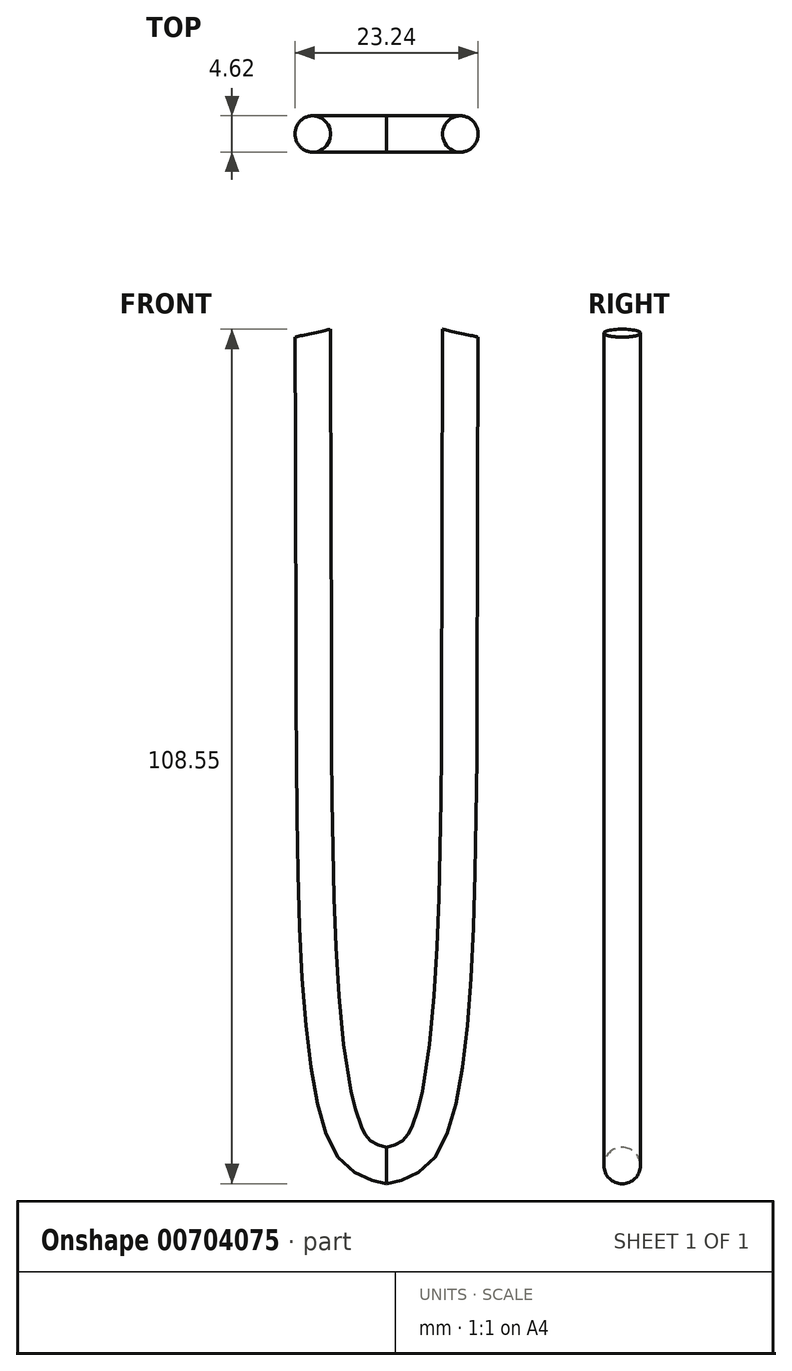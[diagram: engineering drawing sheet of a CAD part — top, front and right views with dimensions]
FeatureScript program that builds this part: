
annotation { "Feature Type Name" : "Feature", "Feature Type Description" : "" }
export const myFeature = defineFeature(function(context is Context, id is Id, definition is map)
    precondition{}
    {
        {
            var Q0;
            Q0=qCreatedBy(makeId("Front.planeOp"),FACE);
            var sketch = newSketch(context, id + "F0", { "sketchPlane" : qUnion([Q0])});
            skFitSpline(sketch, "E0", {"points": [v(0, -64) * mm, v(4.81, -60.84) * mm, v(9.25, 0) * mm, v(9.37, 41.4) * mm, v(9.37, 41.76) * mm], "startDerivative": vector(37.64, 8.71) * mm, "endDerivative": vector(-0.06, 6.2) * mm});
            skFitSpline(sketch, "E1", {"points": [v(9.25, 0) * mm, v(18.47, 12.7) * mm, v(20.22, 30.9) * mm], "startDerivative": vector(21.48, 27.26) * mm, "endDerivative": vector(-0.7, 31.79) * mm});
            skFitSpline(sketch, "E2", {"points": [v(9.08, -23.38) * mm, v(20.34, -21.27) * mm, v(24.42, -10.77) * mm], "startDerivative": vector(24.53, -3.08) * mm, "endDerivative": vector(5.87, 23.46) * mm});
            skSolve(sketch);
        }
        {
            var Q0;
            Q0=qCreatedBy(makeId("Right.planeOp"),FACE);
            var sketch = newSketch(context, id + "F1", { "sketchPlane" : qUnion([Q0])});
            skCircle(sketch, "E3", {"center": v(0, -64) * mm, "radius": 2.31 * mm});
            skSolve(sketch);
        }
        {
            var Q0;
            Q0=makeQuery(id+"F1.imprint","IMPRINT",FACE,{"disambiguationData":[TD([[makeQuery(id+"F1.imprint","IMPRINT",EDGE,{"derivedFrom":sQuery(id+"F1.wireOp",EDGE,"E3")}),1.0]])]});
            var Q1;
            Q1=sQuery(id+"F0.wireOp",EDGE,"E0");
            sweep(context, id + "F2", {"profiles" : qUnion([Q0]), "path" : qUnion([Q1])});
        }
        {
            var Q0;
            Q0=makeQuery(id+"F2.opSweep","SWEPT_BODY",BODY,{"disambiguationData":[OSD([sQuery(id+"F0.wireOp",EDGE,"E0"),sQuery(id+"F1.wireOp",EDGE,"E3")])]});
            var Q1;
            Q1=qCreatedBy(makeId("Right.planeOp"),FACE);
            mirror(context, id + "F3", {"operationType" : NewBodyOperationType.ADD, "entities" : qUnion([Q0]), "mirrorPlane" : qUnion([Q1])});
        }
    });
